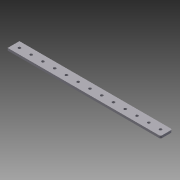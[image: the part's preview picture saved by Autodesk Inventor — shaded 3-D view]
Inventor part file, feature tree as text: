
AUTODESK INVENTOR PART (.ipt)
format: ipt  version: 2014 SP2 (Build 180246200, 246)  size: 137,728 bytes
history: native  units: in
note: dims shown in document units (in); Inventor stores cm internally (conversion verified against a paired STEP export)
features: other x1, extrude x1, imported_body x1, sketch x1
ambient origin geometry x8: Origin, YZ Plane, XZ Plane, XY Plane, X Axis, Y Axis, Z Axis, Center Point
bodies: Solid1 (feature_tree)
feature tree (4):
  other  "288mm Flat Bar.sat1"
  extrude  "Extrusion1"  [1 undecoded]
  imported_body  "Base1"
  sketch  "Sketch1"  dims[d0=0.3937in d1=0.0in]
note: 1 required parameter value undecoded (feature->parameter linkage not recoverable at this tier; creation-order binding heuristic only, values carry confidence <= 0.55)
